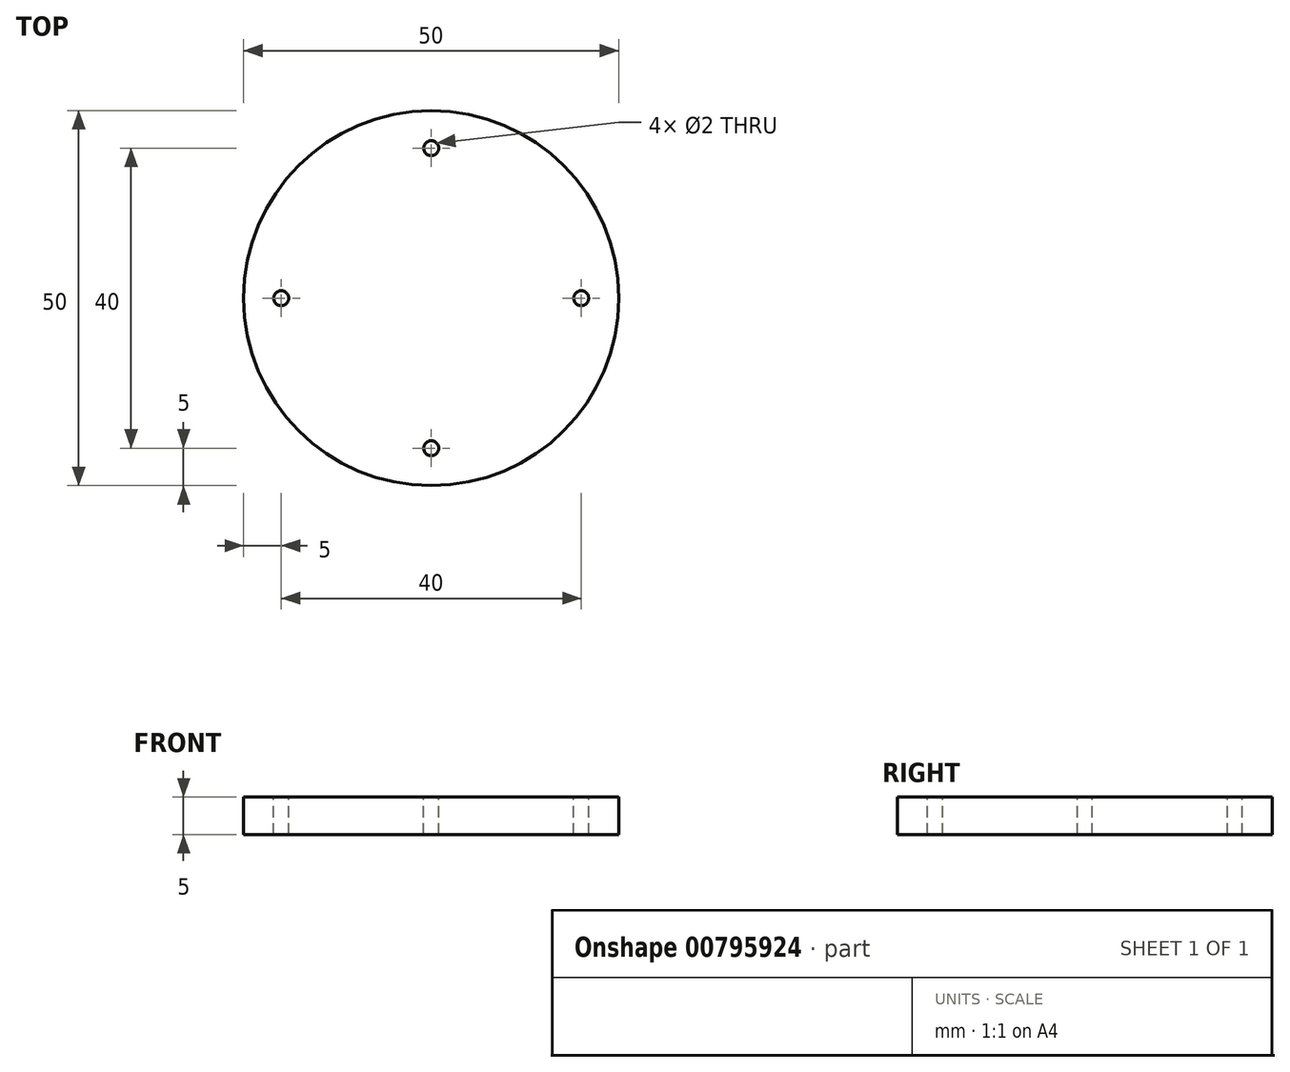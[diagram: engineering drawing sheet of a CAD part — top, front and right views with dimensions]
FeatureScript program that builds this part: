
annotation { "Feature Type Name" : "Feature", "Feature Type Description" : "" }
export const myFeature = defineFeature(function(context is Context, id is Id, definition is map)
    precondition{}
    {
        {
            var Q0;
            Q0=qCreatedBy(makeId("Top.planeOp"),FACE);
            var sketch = newSketch(context, id + "F0", { "sketchPlane" : qUnion([Q0])});
            skCircle(sketch, "E0", {"center": v(0, 0) * mm, "radius": 25 * mm});
            skSolve(sketch);
        }
        {
            var Q0;
            Q0 = qSketchRegion(id + "F0", true);
            extrude(context, id + "F1", {"entities" : qUnion([Q0]), "depth" : 5 * mm, "offsetDistance" : 25 * mm});
        }
        {
            var Q0;
            Q0=makeQuery(id+"F1.opExtrude","CAP_FACE",FACE,{"disambiguationData":[OSD([sQuery(id+"F0.wireOp",EDGE,"E0")])],"isStart":false});
            var sketch = newSketch(context, id + "F2", { "sketchPlane" : qUnion([Q0])});
            skCircle(sketch, "E1", {"center": v(0, 20) * mm, "radius": 1 * mm});
            skCircle(sketch, "E2.1.0", {"center": v(-20, 0) * mm, "radius": 1 * mm});
            skCircle(sketch, "E2.2.0", {"center": v(0, -20) * mm, "radius": 1 * mm});
            skCircle(sketch, "E2.3.0", {"center": v(20, 0) * mm, "radius": 1 * mm});
            skPoint(sketch, "E2.center", {"position": v(0, 0) * mm});
            skSolve(sketch);
        }
        {
            var Q0;
            Q0 = qSketchRegion(id + "F2", true);
            extrude(context, id + "F3", {"entities" : qUnion([Q0]), "operationType" : NewBodyOperationType.REMOVE, "endBound" : BoundingType.THROUGH_ALL, "oppositeDirection" : true, "depth" : 25 * mm, "offsetDistance" : 25 * mm});
        }
    });
